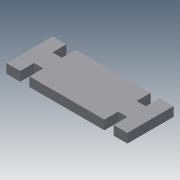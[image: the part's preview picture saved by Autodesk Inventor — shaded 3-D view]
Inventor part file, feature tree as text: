
AUTODESK INVENTOR PART (.ipt)
format: ipt  version: 2013 (Build 170138000, 138)  size: 91,136 bytes
history: native  units: mm
features: extrude x1, sketch x1
ambient origin geometry x8: Origin, YZ Plane, XZ Plane, XY Plane, X Axis, Y Axis, Z Axis, Center Point
bodies: Solid1 (feature_tree)
feature tree (2):
  extrude  "Extrusion1"  Depth=0.4mm
  sketch  "Sketch1"  dims[d0=15.0mm d1=15.0mm d2=15.0mm d3=15.0mm d4=0.4mm d5=0.4mm d6=10.0mm d7=0.0mm]
